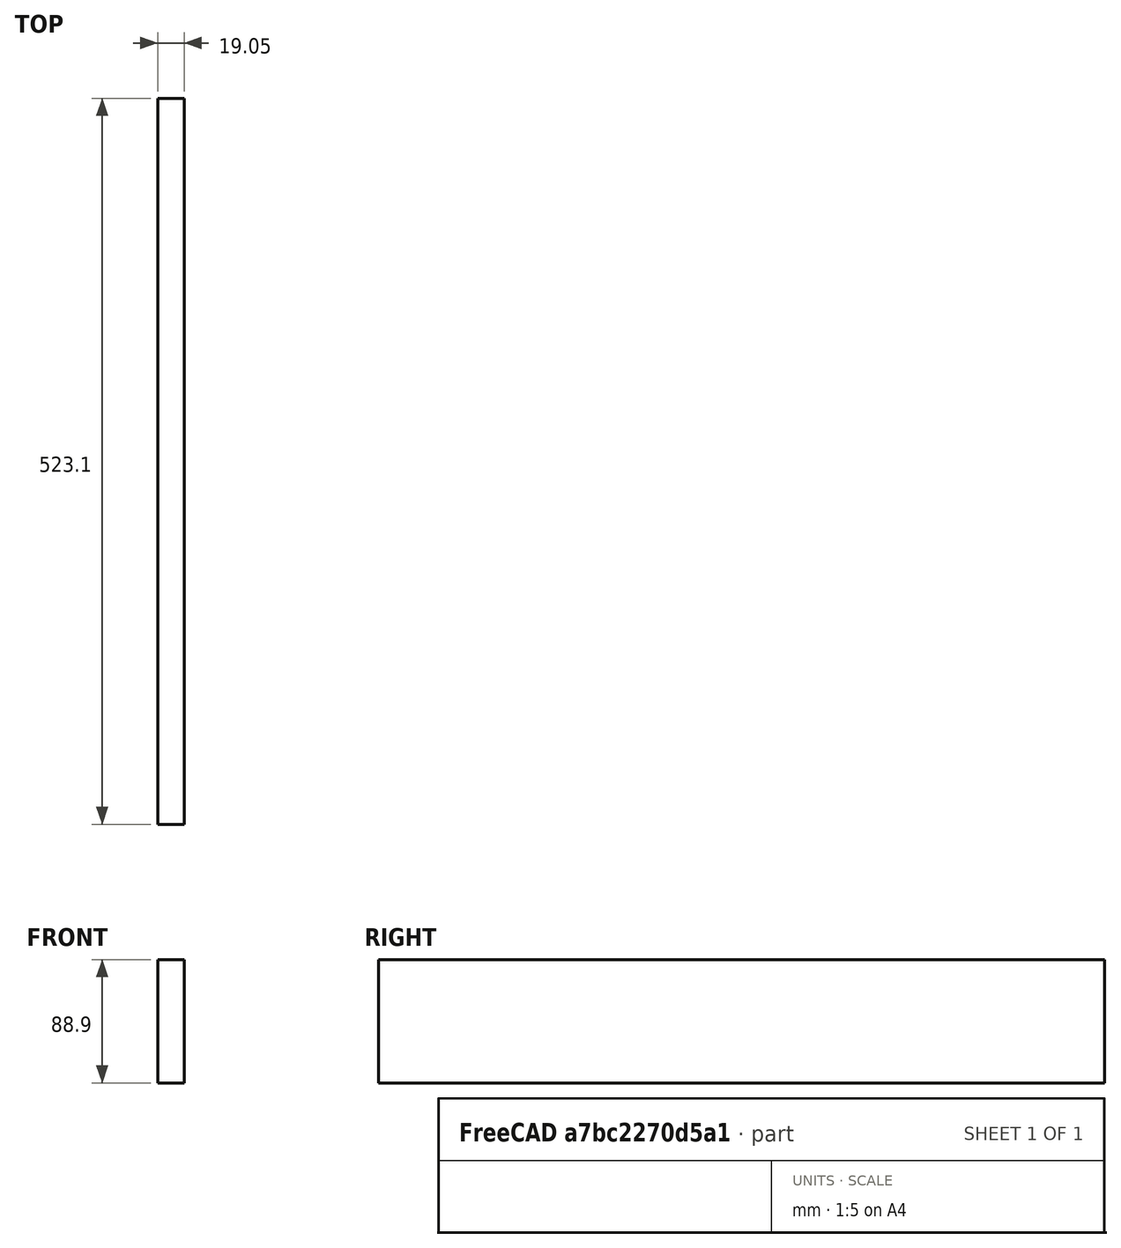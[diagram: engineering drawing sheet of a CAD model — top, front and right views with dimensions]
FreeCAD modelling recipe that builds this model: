
FCSTD DOCUMENT  (FreeCAD 0.19R24291 (Git))
Label: sideFoot
License: All rights reserved
LicenseURL: http://en.wikipedia.org/wiki/All_rights_reserved
objects: Sketcher::SketchObject×1, PartDesign::Pad×1, PartDesign::Body×1
note: 4 computed .brp shape members not serialized (recipe doc carries the construction recipe); baked Part::Feature solids carry a one-line shape summary decoded from their .brp

FEATURE [Sketcher::SketchObject] Sketch
  FullyConstrained = true
  MapMode = 5
  Placement = pos=(0,0,0) rot=(1,0,0;1.5708rad)
  Support = -> [XZ_Plane]
  expr: Constraints[10] = 3 / 4 * 25.4
  expr: Constraints[9] = 3.5 * 25.4
  sketch-geometry (4):
    g0: LineSegment StartX=0 StartY=0 StartZ=0 EndX=19.05 EndY=0 EndZ=0
    g1: LineSegment StartX=19.05 StartY=0 StartZ=0 EndX=19.05 EndY=88.9 EndZ=0
    g2: LineSegment StartX=19.05 StartY=88.9 StartZ=0 EndX=0 EndY=88.9 EndZ=0
    g3: LineSegment StartX=0 StartY=88.9 StartZ=0 EndX=0 EndY=0 EndZ=0
  constraints (11):
    c: Coincident(g0,g1)
    c: Coincident(g1,g2)
    c: Coincident(g2,g3)
    c: Coincident(g3,g0)
    c: Horizontal(g0)
    c: Horizontal(g2)
    c: Vertical(g1)
    c: Vertical(g3)
    c: Coincident(g0,g-1)
    c: DistanceY(g3,g3) = 88.9
    c: DistanceX(g0,g0) = 19.05
FEATURE [PartDesign::Pad] Pad
  Direction = (1,1,1)
  Length = 523.1
  Length2 = 100
  Placement = pos=(0,0,0) rot=(1,0,0;1.5708rad)
  Profile = -> Sketch
  Type = 0
  expr: Length = 523.1
FEATURE [PartDesign::Body] Body
  Group = -> [Sketch,Pad]
  Origin = -> Origin
  Tip = -> Pad
